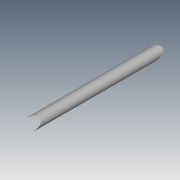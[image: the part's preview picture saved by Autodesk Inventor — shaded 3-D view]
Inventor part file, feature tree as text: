
AUTODESK INVENTOR PART (.ipt)
format: ipt  version: 2015 (Build 190159000, 159)  size: 68,608 bytes
history: native  units: mm
features: extrude x1, sketch x1
ambient origin geometry x8: Origin, YZ Plane, XZ Plane, XY Plane, X Axis, Y Axis, Z Axis, Center Point
bodies: Solid1 (feature_tree)
feature tree (2):
  extrude  "Extrusion1"  Depth=140.0mm TaperAngle=0.0deg
  sketch  "Sketch1"  dims[d0=10.0mm d1=140.0mm d2=0.0mm]
